# Revit family: ISI_IdealStandard_Baths_Dea-FreeStanding_E3066
name_source: partatom
category: Plumbing Fixtures
revit_build: Autodesk Revit MEP 2012 (Build: 20110309_2315(x64)
units: mm (PartAtom-declared; Revit-internal decimal feet)

## types (1)
- E306601 - Dea 170 x 75cm Freestanding double-ended bath
    Accessories = www.idealspec.co.uk
    AreaUnits = millimeters
    Assembly Code = C1030200
    AssetType = Fixed
    BIMObjectName = ISI_IdealStandard_Baths_Dea_E3066
    BREEAM = No
    BathType = Domestic
    Brand = Ideal Standard
    CWFU = 0
    Color = White
    ConnectionType = PLUMBING
    Default Elevation = 1219 mm
    Description = Dea 170 x 75 cm freestanding double-ended bath
    DrainSize = 38 mm
    DurationUnit = year
    ECA = No
    ExpectedLife = 30
    Features = Freestanding double-ended bath
    Finish = White
    HWFU = 0
    HasGrabHandles = No
    IfcExportAs = IfcSanitaryTerminalType
    IfcExportType = BATH
    InstallationInstructions = www.idealspec.co.uk/resources.html
    LinearUnits = millimeters
    ManufacturerURL = www.idealspec.co.uk
    Material = Acrylic
    MaterialThickness = 0 mm  [stored 0 ft]
    Model = E306601
    ModelNumber = E306601
    ModelReference = Dea 170 x 75 cm freestanding double-ended bath
    NBSDescription = Baths
    NBSReference = 45-35-70/311
    Name = Baths_Dea_E3066_IdealStandard
    NettWeight = 54 Kg
    NominalDepth = 745 mm
    NominalHeight = 611 mm
    NominalLength = 1700 mm
    NominalWidth = 745 mm
    ProductInformation = www.idealspec.co.uk/datasheets/E306601
    Shape = Elliptical
    Size = 610 x 1700 x 745 mm
    Space = Internal
    SpareParts = www.fastpart-spares.co.uk
    TMV3 = No
    URL = www.idealspec.co.uk
    Uniclass2 = Pr_40_20_06_08
    Version = 2
    VolumeUnits = Litres
    WFU = 0
    WRAS = No
    WarrantyDescription = Manufacturers warranty
    WarrantyDurationParts = 25
    WarrantyDurationUnit = year
    WaterEfficientProduct = No

note: [stored X ft] marks values corroborated as IEEE doubles in the binary element streams (Revit-internal decimal feet)

## geometry (parser evidence)
native form markers: Sweep x3
no freeform markers — native parametric forms only
